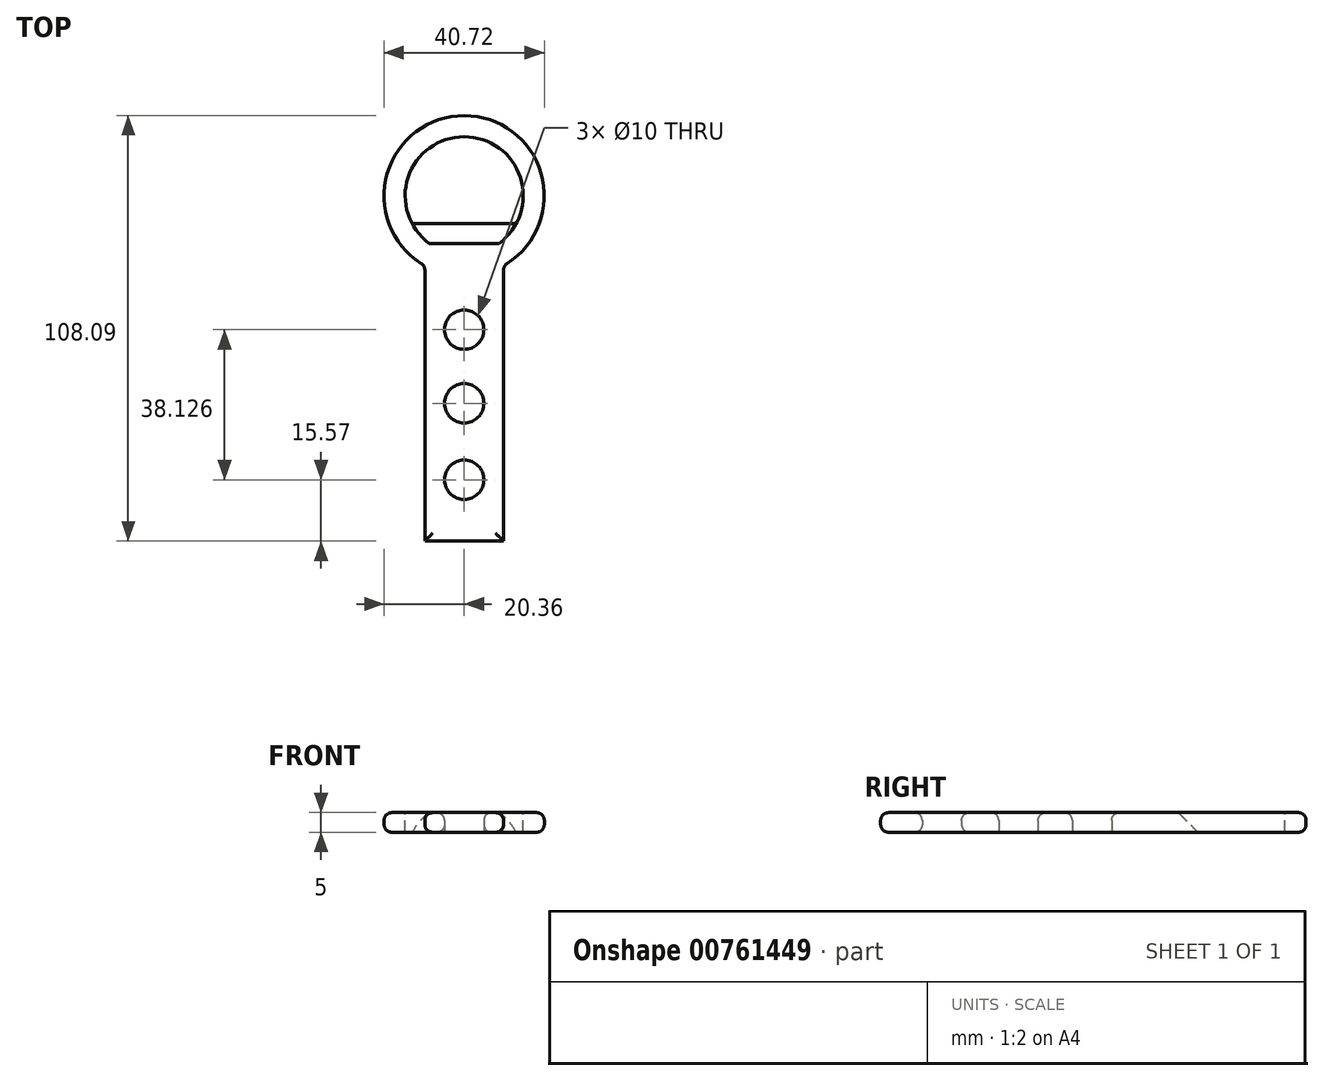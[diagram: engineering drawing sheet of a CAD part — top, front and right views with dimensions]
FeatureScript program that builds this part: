
annotation { "Feature Type Name" : "Feature", "Feature Type Description" : "" }
export const myFeature = defineFeature(function(context is Context, id is Id, definition is map)
    precondition{}
    {
        {
            var Q0;
            Q0=qCreatedBy(makeId("Top.planeOp"),FACE);
            var sketch = newSketch(context, id + "F0", { "sketchPlane" : qUnion([Q0])});
            skLineSegment(sketch, "E0.bottom", {"start": v(10, -35) * mm, "end": v(-10, -35) * mm});
            skLineSegment(sketch, "E0.left", {"start": v(10, -35) * mm, "end": v(10, 35) * mm});
            skLineSegment(sketch, "E0.right", {"start": v(-10, -35) * mm, "end": v(-10, 35) * mm});
            skPoint(sketch, "E0.middle", {"position": v(0, 0) * mm});
            skArc(sketch, "E1", {"start": v(10, 35) * mm, "mid": v(0, 73.1) * mm, "end": v(-10, 35) * mm});
            skSolve(sketch);
        }
        {
            var Q0;
            Q0=makeQuery(id+"F0.imprint","IMPRINT",FACE,{"disambiguationData":[TD([[makeQuery(id+"F0.imprint","IMPRINT",EDGE,{"derivedFrom":sQuery(id+"F0.wireOp",EDGE,"E0.bottom")}),-1.0]])]});
            extrude(context, id + "F1", {"entities" : qUnion([Q0]), "depth" : 5 * mm, "offsetDistance" : 25.4 * mm});
        }
        {
            var Q0;
            Q0=makeQuery(id+"F1.opExtrude","CAP_EDGE",EDGE,{"disambiguationData":[OSD([sQuery(id+"F0.wireOp",EDGE,"E1")])],"isStart":false});
            var Q1;
            Q1=makeQuery(id+"F1.opExtrude","CAP_EDGE",EDGE,{"disambiguationData":[OSD([sQuery(id+"F0.wireOp",EDGE,"E0.left")])],"isStart":false});
            var Q2;
            Q2=makeQuery(id+"F1.opExtrude","CAP_FACE",FACE,{"disambiguationData":[OSD([sQuery(id+"F0.wireOp",EDGE,"E0.bottom"),sQuery(id+"F0.wireOp",EDGE,"E0.left"),sQuery(id+"F0.wireOp",EDGE,"E0.right"),sQuery(id+"F0.wireOp",EDGE,"E1")])],"isStart":false});
            var Q3;
            Q3=makeQuery(id+"F1.opExtrude","CAP_EDGE",EDGE,{"disambiguationData":[OSD([sQuery(id+"F0.wireOp",EDGE,"E0.left")])],"isStart":true});
            var Q4;
            Q4=makeQuery(id+"F1.opExtrude","CAP_EDGE",EDGE,{"disambiguationData":[OSD([sQuery(id+"F0.wireOp",EDGE,"E1")])],"isStart":true});
            var Q5;
            Q5=makeQuery(id+"F1.opExtrude","CAP_EDGE",EDGE,{"disambiguationData":[OSD([sQuery(id+"F0.wireOp",EDGE,"E0.right")])],"isStart":true});
            var Q6;
            Q6=makeQuery(id+"F1.opExtrude","SWEPT_EDGE",EDGE,{"disambiguationData":[OSD([sQuery(id+"F0.wireOp",EDGE,"E0.right"),sQuery(id+"F0.wireOp",EDGE,"E1")])]});
            var Q7;
            Q7=makeQuery(id+"F1.opExtrude","SWEPT_EDGE",EDGE,{"disambiguationData":[OSD([sQuery(id+"F0.wireOp",EDGE,"E0.left"),sQuery(id+"F0.wireOp",EDGE,"E1")])]});
            var Q8;
            Q8=makeQuery(id+"F1.opExtrude","CAP_EDGE",EDGE,{"disambiguationData":[OSD([sQuery(id+"F0.wireOp",EDGE,"E0.bottom")])],"isStart":false});
            var Q9;
            Q9=makeQuery(id+"F1.opExtrude","CAP_EDGE",EDGE,{"disambiguationData":[OSD([sQuery(id+"F0.wireOp",EDGE,"E0.bottom")])],"isStart":true});
            fillet(context, id + "F2", {"entities" : qUnion([Q0, Q1, Q2, Q3, Q4, Q5, Q6, Q7, Q8, Q9]), "radius" : 2 * mm, "tangentPropagation" : true, "allowEdgeOverflow" : false});
        }
        {
            var Q0;
            Q0=makeQuery(id+"F1.opExtrude","CAP_FACE",FACE,{"disambiguationData":[OSD([sQuery(id+"F0.wireOp",EDGE,"E0.bottom"),sQuery(id+"F0.wireOp",EDGE,"E0.left"),sQuery(id+"F0.wireOp",EDGE,"E0.right"),sQuery(id+"F0.wireOp",EDGE,"E1")])],"isStart":false});
            var sketch = newSketch(context, id + "F3", { "sketchPlane" : qUnion([Q0])});
            skCircle(sketch, "E2", {"center": v(0, 52.73) * mm, "radius": 15 * mm});
            skSolve(sketch);
        }
        {
            var Q0;
            Q0=makeQuery(id+"F3.imprint","IMPRINT",FACE,{"disambiguationData":[TD([[makeQuery(id+"F3.imprint","IMPRINT",EDGE,{"derivedFrom":sQuery(id+"F3.wireOp",EDGE,"E2")}),1.0]])]});
            extrude(context, id + "F4", {"entities" : qUnion([Q0]), "operationType" : NewBodyOperationType.REMOVE, "oppositeDirection" : true, "depth" : 25.4 * mm, "offsetDistance" : 25.4 * mm});
        }
        {
            var Q0;
            Q0=makeQuery(id+"FePDNmbGhS1i7yE_1.boolean.opBoolean","MERGE",FACE,{"derivedFrom":[makeQuery(id+"F1.opExtrude","CAP_FACE",FACE,{"disambiguationData":[OSD([sQuery(id+"F0.wireOp",EDGE,"E0.bottom"),sQuery(id+"F0.wireOp",EDGE,"E0.left"),sQuery(id+"F0.wireOp",EDGE,"E0.right"),sQuery(id+"F0.wireOp",EDGE,"E1")])],"isStart":true}),makeQuery(id+"FePDNmbGhS1i7yE_1.opExtrude","CAP_FACE",FACE,{"disambiguationData":[OSD([sQuery(id+"FaZYkTNNAdtalAh_1.wireOp",EDGE,"vf7hJe8z-B1In-xPVu-U8Be-I9CYwWhbT8ot.bottom"),sQuery(id+"FaZYkTNNAdtalAh_1.wireOp",EDGE,"vf7hJe8z-B1In-xPVu-U8Be-I9CYwWhbT8ot.top"),sQuery(id+"FaZYkTNNAdtalAh_1.wireOp",EDGE,"vf7hJe8z-B1In-xPVu-U8Be-I9CYwWhbT8ot.left"),sQuery(id+"FaZYkTNNAdtalAh_1.wireOp",EDGE,"vf7hJe8z-B1In-xPVu-U8Be-I9CYwWhbT8ot.right")])],"isStart":false})]});
            var sketch = newSketch(context, id + "F5", { "sketchPlane" : qUnion([Q0])});
            skCircle(sketch, "E3", {"center": v(0, 0) * mm, "radius": 5 * mm});
            skCircle(sketch, "E4", {"center": v(0, 19.43) * mm, "radius": 5 * mm});
            skCircle(sketch, "E5", {"center": v(0, -18.7) * mm, "radius": 5 * mm});
            skSolve(sketch);
        }
        {
            var Q0;
            Q0=makeQuery(id+"F5.imprint","IMPRINT",FACE,{"disambiguationData":[TD([[makeQuery(id+"F5.imprint","IMPRINT",EDGE,{"derivedFrom":sQuery(id+"F5.wireOp",EDGE,"E3")}),1.0]])]});
            var Q1;
            Q1=makeQuery(id+"F5.imprint","IMPRINT",FACE,{"disambiguationData":[TD([[makeQuery(id+"F5.imprint","IMPRINT",EDGE,{"derivedFrom":sQuery(id+"F5.wireOp",EDGE,"E5")}),1.0]])]});
            var Q2;
            Q2=makeQuery(id+"F5.imprint","IMPRINT",FACE,{"disambiguationData":[TD([[makeQuery(id+"F5.imprint","IMPRINT",EDGE,{"derivedFrom":sQuery(id+"F5.wireOp",EDGE,"E4")}),1.0]])]});
            extrude(context, id + "F6", {"entities" : qUnion([Q0, Q1, Q2]), "operationType" : NewBodyOperationType.REMOVE, "oppositeDirection" : true, "depth" : 25.4 * mm, "offsetDistance" : 25.4 * mm});
        }
        {
            var Q0;
            Q0=makeQuery(id+"F6.boolean.opBoolean","INTERSECT",EDGE,{"derivedFrom":[makeQuery(id+"FePDNmbGhS1i7yE_1.boolean.opBoolean","MERGE",FACE,{"derivedFrom":[makeQuery(id+"F1.opExtrude","CAP_FACE",FACE,{"disambiguationData":[OSD([sQuery(id+"F0.wireOp",EDGE,"E0.bottom"),sQuery(id+"F0.wireOp",EDGE,"E0.left"),sQuery(id+"F0.wireOp",EDGE,"E0.right"),sQuery(id+"F0.wireOp",EDGE,"E1")])],"isStart":false}),makeQuery(id+"FePDNmbGhS1i7yE_1.opExtrude","CAP_FACE",FACE,{"disambiguationData":[OSD([sQuery(id+"FaZYkTNNAdtalAh_1.wireOp",EDGE,"vf7hJe8z-B1In-xPVu-U8Be-I9CYwWhbT8ot.bottom"),sQuery(id+"FaZYkTNNAdtalAh_1.wireOp",EDGE,"vf7hJe8z-B1In-xPVu-U8Be-I9CYwWhbT8ot.top"),sQuery(id+"FaZYkTNNAdtalAh_1.wireOp",EDGE,"vf7hJe8z-B1In-xPVu-U8Be-I9CYwWhbT8ot.left"),sQuery(id+"FaZYkTNNAdtalAh_1.wireOp",EDGE,"vf7hJe8z-B1In-xPVu-U8Be-I9CYwWhbT8ot.right")])],"isStart":true})]}),makeQuery(id+"F6.opExtrude","SWEPT_FACE",FACE,{"disambiguationData":[OSD([sQuery(id+"F5.wireOp",EDGE,"E5")])]})]});
            var Q1;
            Q1=makeQuery(id+"F6.boolean.opBoolean","INTERSECT",EDGE,{"derivedFrom":[makeQuery(id+"FePDNmbGhS1i7yE_1.boolean.opBoolean","MERGE",FACE,{"derivedFrom":[makeQuery(id+"F1.opExtrude","CAP_FACE",FACE,{"disambiguationData":[OSD([sQuery(id+"F0.wireOp",EDGE,"E0.bottom"),sQuery(id+"F0.wireOp",EDGE,"E0.left"),sQuery(id+"F0.wireOp",EDGE,"E0.right"),sQuery(id+"F0.wireOp",EDGE,"E1")])],"isStart":false}),makeQuery(id+"FePDNmbGhS1i7yE_1.opExtrude","CAP_FACE",FACE,{"disambiguationData":[OSD([sQuery(id+"FaZYkTNNAdtalAh_1.wireOp",EDGE,"vf7hJe8z-B1In-xPVu-U8Be-I9CYwWhbT8ot.bottom"),sQuery(id+"FaZYkTNNAdtalAh_1.wireOp",EDGE,"vf7hJe8z-B1In-xPVu-U8Be-I9CYwWhbT8ot.top"),sQuery(id+"FaZYkTNNAdtalAh_1.wireOp",EDGE,"vf7hJe8z-B1In-xPVu-U8Be-I9CYwWhbT8ot.left"),sQuery(id+"FaZYkTNNAdtalAh_1.wireOp",EDGE,"vf7hJe8z-B1In-xPVu-U8Be-I9CYwWhbT8ot.right")])],"isStart":true})]}),makeQuery(id+"F6.opExtrude","SWEPT_FACE",FACE,{"disambiguationData":[OSD([sQuery(id+"F5.wireOp",EDGE,"E3")])]})]});
            var Q2;
            Q2=makeQuery(id+"F6.boolean.opBoolean","INTERSECT",EDGE,{"derivedFrom":[makeQuery(id+"FePDNmbGhS1i7yE_1.boolean.opBoolean","MERGE",FACE,{"derivedFrom":[makeQuery(id+"F1.opExtrude","CAP_FACE",FACE,{"disambiguationData":[OSD([sQuery(id+"F0.wireOp",EDGE,"E0.bottom"),sQuery(id+"F0.wireOp",EDGE,"E0.left"),sQuery(id+"F0.wireOp",EDGE,"E0.right"),sQuery(id+"F0.wireOp",EDGE,"E1")])],"isStart":false}),makeQuery(id+"FePDNmbGhS1i7yE_1.opExtrude","CAP_FACE",FACE,{"disambiguationData":[OSD([sQuery(id+"FaZYkTNNAdtalAh_1.wireOp",EDGE,"vf7hJe8z-B1In-xPVu-U8Be-I9CYwWhbT8ot.bottom"),sQuery(id+"FaZYkTNNAdtalAh_1.wireOp",EDGE,"vf7hJe8z-B1In-xPVu-U8Be-I9CYwWhbT8ot.top"),sQuery(id+"FaZYkTNNAdtalAh_1.wireOp",EDGE,"vf7hJe8z-B1In-xPVu-U8Be-I9CYwWhbT8ot.left"),sQuery(id+"FaZYkTNNAdtalAh_1.wireOp",EDGE,"vf7hJe8z-B1In-xPVu-U8Be-I9CYwWhbT8ot.right")])],"isStart":true})]}),makeQuery(id+"F6.opExtrude","SWEPT_FACE",FACE,{"disambiguationData":[OSD([sQuery(id+"F5.wireOp",EDGE,"E4")])]})]});
            var Q3;
            Q3=makeQuery(id+"F6.boolean.opBoolean","COPY",FACE,{"derivedFrom":makeQuery(id+"F6.opExtrude","SWEPT_FACE",FACE,{"disambiguationData":[OSD([sQuery(id+"F5.wireOp",EDGE,"E4")])]})});
            fillet(context, id + "F7", {"entities" : qUnion([Q0, Q1, Q2, Q3]), "radius" : 2 * mm, "tangentPropagation" : true, "allowEdgeOverflow" : false});
        }
        {
            var Q0;
            Q0=makeQuery(id+"F1.opExtrude","CAP_FACE",FACE,{"disambiguationData":[OSD([sQuery(id+"F0.wireOp",EDGE,"E0.bottom"),sQuery(id+"F0.wireOp",EDGE,"E0.left"),sQuery(id+"F0.wireOp",EDGE,"E0.right"),sQuery(id+"F0.wireOp",EDGE,"E1")])],"isStart":true});
            var sketch = newSketch(context, id + "F8", { "sketchPlane" : qUnion([Q0])});
            skLineSegment(sketch, "E6", {"start": v(-13.21, -45.63) * mm, "end": v(13.21, -45.63) * mm});
            skArc(sketch, "E7", {"start": v(13.21, -45.63) * mm, "mid": v(0, -37.29) * mm, "end": v(-13.21, -45.63) * mm});
            skSolve(sketch);
        }
        {
            var Q0;
            {var subQ0=sQuery(id+"F8.wireOp",EDGE,"E6");Q0=makeQuery(id+"F8.imprint","IMPRINT",FACE,{"disambiguationData":[TD([[makeQuery(id+"F8.imprint","IMPRINT",EDGE,{"derivedFrom":subQ0}),1.0]])]});}
            extrude(context, id + "F9", {"entities" : qUnion([Q0]), "operationType" : NewBodyOperationType.ADD, "oppositeDirection" : true, "depth" : 5 * mm, "offsetDistance" : 25.4 * mm});
        }
        {
            var Q0;
            Q0=makeQuery(id+"F9.opExtrude","CAP_EDGE",EDGE,{"disambiguationData":[OSD([sQuery(id+"F8.wireOp",EDGE,"E6")])],"isStart":false});
            chamfer(context, id + "F10", {"entities" : qUnion([Q0]), "width" : 5 * mm, "tangentPropagation" : true});
        }
    });
